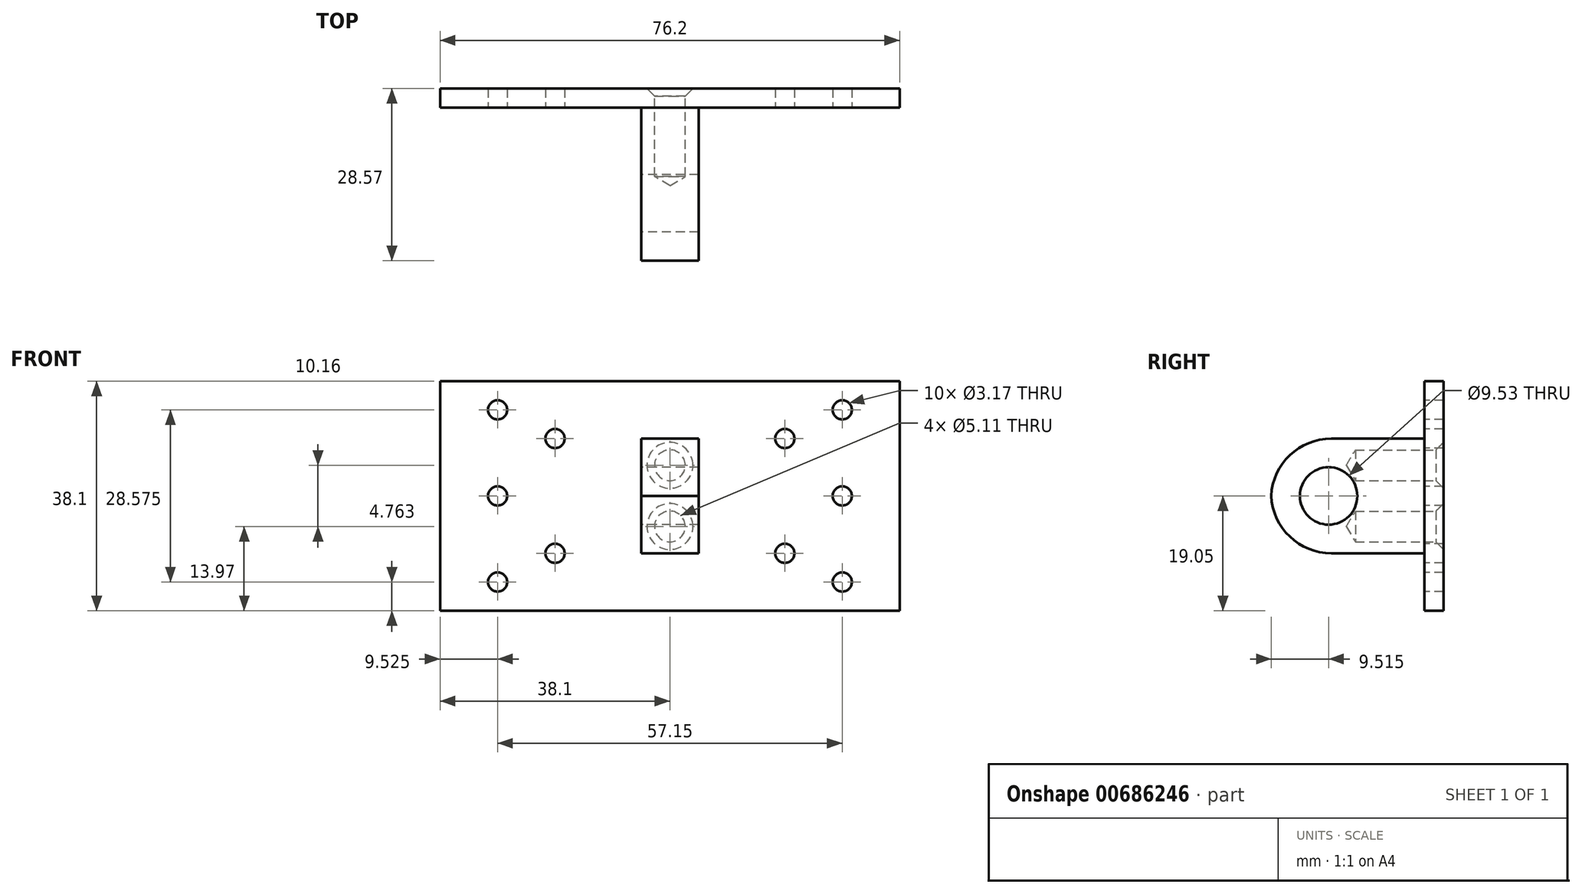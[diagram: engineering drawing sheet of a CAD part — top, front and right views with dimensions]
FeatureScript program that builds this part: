
annotation { "Feature Type Name" : "Feature", "Feature Type Description" : "" }
export const myFeature = defineFeature(function(context is Context, id is Id, definition is map)
    precondition{}
    {
        {
            var Q0;
            Q0=qCreatedBy(makeId("Right.planeOp"),FACE);
            var sketch = newSketch(context, id + "F0", { "sketchPlane" : qUnion([Q0])});
            skLineSegment(sketch, "E0.bottom", {"start": v(-12.7, 9.52) * mm, "end": v(12.7, 9.52) * mm});
            skLineSegment(sketch, "E0.top", {"start": v(-12.7, -9.53) * mm, "end": v(12.7, -9.53) * mm});
            skLineSegment(sketch, "E0.left", {"start": v(-12.7, 9.52) * mm, "end": v(-12.7, -9.53) * mm});
            skLineSegment(sketch, "E0.right", {"start": v(12.7, 9.52) * mm, "end": v(12.7, -9.53) * mm});
            skPoint(sketch, "E0.middle", {"position": v(0, 0) * mm});
            skLineSegment(sketch, "E1", {"start": v(-12.7, 0) * mm, "end": v(-3.18, 0) * mm, "construction": true});
            skPoint(sketch, "E2", {"position": v(-3.18, 0) * mm});
            skCircle(sketch, "E3", {"center": v(-3.18, 0) * mm, "radius": 4.76 * mm});
            skSolve(sketch);
        }
        {
            var Q0;
            Q0 = qSketchRegion(id + "F0", true);
            extrude(context, id + "F1", {"entities" : qUnion([Q0]), "endBound" : BoundingType.SYMMETRIC, "depth" : 9.52 * mm, "offsetDistance" : 25.4 * mm});
        }
        {
            var Q0;
            Q0=makeQuery(id+"F1.opExtrude","SWEPT_EDGE",EDGE,{"disambiguationData":[OSD([sQuery(id+"F0.wireOp",EDGE,"E0.bottom"),sQuery(id+"F0.wireOp",EDGE,"E0.left")])]});
            var Q1;
            Q1=makeQuery(id+"F1.opExtrude","SWEPT_EDGE",EDGE,{"disambiguationData":[OSD([sQuery(id+"F0.wireOp",EDGE,"E0.top"),sQuery(id+"F0.wireOp",EDGE,"E0.left")])]});
            fillet(context, id + "F2", {"entities" : qUnion([Q0, Q1]), "radius" : 10 * mm, "tangentPropagation" : true, "allowEdgeOverflow" : false});
        }
        {
            var Q0;
            Q0=makeQuery(id+"F1.opExtrude","SWEPT_FACE",FACE,{"disambiguationData":[OSD([sQuery(id+"F0.wireOp",EDGE,"E0.right")])]});
            var sketch = newSketch(context, id + "F3", { "sketchPlane" : qUnion([Q0])});
            skLineSegment(sketch, "E4.bottom", {"start": v(38.1, -19.05) * mm, "end": v(-38.1, -19.05) * mm});
            skLineSegment(sketch, "E4.top", {"start": v(38.1, 19.05) * mm, "end": v(-38.1, 19.05) * mm});
            skLineSegment(sketch, "E4.left", {"start": v(38.1, -19.05) * mm, "end": v(38.1, 19.05) * mm});
            skLineSegment(sketch, "E4.right", {"start": v(-38.1, -19.05) * mm, "end": v(-38.1, 19.05) * mm});
            skPoint(sketch, "E4.middle", {"position": v(0, 0) * mm});
            skPoint(sketch, "E4.middle.positionSnap0", {"position": v(0, 9.53) * mm});
            skPoint(sketch, "E4.middle.positionSnap1", {"position": v(-4.76, 0) * mm});
            skPoint(sketch, "E4.centerSnap0", {"position": v(0, 9.53) * mm});
            skPoint(sketch, "E4.centerSnap1", {"position": v(-4.76, 0) * mm});
            skLineSegment(sketch, "E5", {"start": v(-38.1, 0) * mm, "end": v(38.1, 0) * mm, "construction": true});
            skLineSegment(sketch, "E6", {"start": v(0, 19.05) * mm, "end": v(0, -19.05) * mm, "construction": true});
            skLineSegment(sketch, "E7", {"start": v(38.1, 19.05) * mm, "end": v(-38.1, -19.05) * mm, "construction": true});
            skLineSegment(sketch, "E8", {"start": v(-38.1, 19.05) * mm, "end": v(38.1, -19.05) * mm, "construction": true});
            skLineSegment(sketch, "E9", {"start": v(-38.1, 19.05) * mm, "end": v(-19.05, 19.05) * mm, "construction": true});
            skLineSegment(sketch, "E10", {"start": v(-19.05, 19.05) * mm, "end": v(-19.05, -23.23) * mm, "construction": true});
            skLineSegment(sketch, "E11", {"start": v(38.1, 19.05) * mm, "end": v(19.05, 19.05) * mm, "construction": true});
            skLineSegment(sketch, "E12", {"start": v(19.05, 19.05) * mm, "end": v(19.05, -31.4) * mm, "construction": true});
            skCircle(sketch, "E13", {"center": v(-19.05, 9.52) * mm, "radius": 1.59 * mm});
            skCircle(sketch, "E14", {"center": v(-19.05, -9.52) * mm, "radius": 1.59 * mm});
            skCircle(sketch, "E15", {"center": v(-28.58, 0) * mm, "radius": 1.59 * mm});
            skPoint(sketch, "E15.centerSnap0", {"position": v(-28.58, 19.05) * mm});
            skCircle(sketch, "E16", {"center": v(-28.58, 14.29) * mm, "radius": 1.59 * mm});
            skCircle(sketch, "E17", {"center": v(-28.58, -14.29) * mm, "radius": 1.59 * mm});
            skPoint(sketch, "E18.MirrorP", {"position": v(28.57, 19.05) * mm});
            skCircle(sketch, "E19.MirrorC", {"center": v(28.58, 14.29) * mm, "radius": 1.59 * mm});
            skCircle(sketch, "E20.MirrorC", {"center": v(28.58, -14.29) * mm, "radius": 1.59 * mm});
            skCircle(sketch, "E21.MirrorC", {"center": v(28.58, 0) * mm, "radius": 1.59 * mm});
            skCircle(sketch, "E22.MirrorC", {"center": v(19.05, -9.52) * mm, "radius": 1.59 * mm});
            skCircle(sketch, "E23.MirrorC", {"center": v(19.05, 9.52) * mm, "radius": 1.59 * mm});
            skSolve(sketch);
        }
        {
            var Q0;
            Q0=makeQuery(id+"F3.imprint","IMPRINT",FACE,{"disambiguationData":[TD([[makeQuery(id+"F3.imprint","IMPRINT",EDGE,{"derivedFrom":sQuery(id+"F3.wireOp",EDGE,"E4.bottom")}),-1.0]])]});
            var Q1;
            {var subQ0=sQuery(id+"F0.wireOp",EDGE,"E0.right");Q1=makeQuery(id+"F3.imprint","IMPRINT",FACE,{"disambiguationData":[TD([[makeQuery(id+"F3.imprint","IMPRINT",EDGE,{"derivedFrom":makeQuery(id+"F1.opExtrude","CAP_EDGE",EDGE,{"disambiguationData":[OSD([subQ0])],"isStart":true})}),-1.0]])]});}
            extrude(context, id + "F4", {"entities" : qUnion([Q0, Q1]), "depth" : 3.17 * mm, "offsetDistance" : 25.4 * mm});
        }
        {
            var Q0;
            Q0=makeQuery(id+"F4.opExtrude","CAP_FACE",FACE,{"disambiguationData":[OSD([sQuery(id+"F3.wireOp",EDGE,"E4.bottom"),sQuery(id+"F3.wireOp",EDGE,"E4.top"),sQuery(id+"F3.wireOp",EDGE,"E4.right"),sQuery(id+"F3.wireOp",EDGE,"E13"),sQuery(id+"F3.wireOp",EDGE,"E14"),sQuery(id+"F3.wireOp",EDGE,"E15"),sQuery(id+"F3.wireOp",EDGE,"E16"),sQuery(id+"F3.wireOp",EDGE,"E17"),sQuery(id+"F3.wireOp",EDGE,"E19.MirrorC"),sQuery(id+"F3.wireOp",EDGE,"E20.MirrorC"),sQuery(id+"F3.wireOp",EDGE,"E21.MirrorC"),sQuery(id+"F3.wireOp",EDGE,"E4.left"),sQuery(id+"F3.wireOp",EDGE,"E22.MirrorC"),sQuery(id+"F3.wireOp",EDGE,"E23.MirrorC")])],"isStart":false});
            var sketch = newSketch(context, id + "F5", { "sketchPlane" : qUnion([Q0])});
            skCircle(sketch, "E24", {"center": v(0, -5.08) * mm, "radius": 1.13 * mm});
            skCircle(sketch, "E25.MirrorC", {"center": v(0, 5.08) * mm, "radius": 1.13 * mm});
            skSolve(sketch);
        }
        {
            var Q0;
            Q0=sQuery(id+"F5.wireOp",VERTEX,"E24.center");
            var Q1;
            Q1=sQuery(id+"F5.wireOp",VERTEX,"E25.MirrorC.center");
            var Q2;
            Q2=makeQuery(id+"F1.opExtrude","SWEPT_BODY",BODY,{"disambiguationData":[OSD([sQuery(id+"F0.wireOp",EDGE,"E0.bottom"),sQuery(id+"F0.wireOp",EDGE,"E0.top"),sQuery(id+"F0.wireOp",EDGE,"E0.left"),sQuery(id+"F0.wireOp",EDGE,"E0.right"),sQuery(id+"F0.wireOp",EDGE,"E3")])]});
            var Q3;
            Q3=makeQuery(id+"F4.opExtrude","SWEPT_BODY",BODY,{"disambiguationData":[OSD([sQuery(id+"F3.wireOp",EDGE,"E4.bottom"),sQuery(id+"F3.wireOp",EDGE,"E4.top"),sQuery(id+"F3.wireOp",EDGE,"E4.right"),sQuery(id+"F3.wireOp",EDGE,"E13"),sQuery(id+"F3.wireOp",EDGE,"E14"),sQuery(id+"F3.wireOp",EDGE,"E15"),sQuery(id+"F3.wireOp",EDGE,"E16"),sQuery(id+"F3.wireOp",EDGE,"E17"),sQuery(id+"F3.wireOp",EDGE,"E19.MirrorC"),sQuery(id+"F3.wireOp",EDGE,"E20.MirrorC"),sQuery(id+"F3.wireOp",EDGE,"E21.MirrorC"),sQuery(id+"F3.wireOp",EDGE,"E4.left"),sQuery(id+"F3.wireOp",EDGE,"E22.MirrorC"),sQuery(id+"F3.wireOp",EDGE,"E23.MirrorC")])]});
            hole(context, id + "F6", {"style" : HoleStyle.C_SINK, "endStyle" : HoleEndStyle.BLIND_IN_LAST, "holeDiameter" : 5.1 * mm, "cSinkDiameter" : 7.62 * mm, "cSinkAngle" : 90 * degree, "tapDrillDiameter" : 5.1 * mm, "majorDiameter" : 6.35 * mm, "holeDepth" : 11.43 * mm, "isTappedThrough" : true, "tappedDepth" : 12.7 * mm, "tapClearance" : 3, "locations" : qUnion([Q0, Q1]), "scope" : qUnion([Q2, Q3])});
        }
    });
